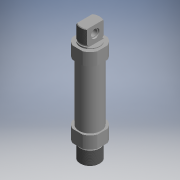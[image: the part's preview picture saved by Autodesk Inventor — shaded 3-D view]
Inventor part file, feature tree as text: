
AUTODESK INVENTOR PART (.ipt)
format: ipt  version: 2017.3 (Build 213256000, 256)  size: 256,512 bytes
history: native  units: mm (DEFAULTED — no unit token found)
features: other x70, sketch x7, revolve x3, thread x2, extrude x2, hole x2
ambient origin geometry x8: Origin, YZ Plane, XZ Plane, XY Plane, X Axis, Y Axis, Z Axis, Center Point
bodies: Solid1 (feature_tree)
feature tree (86):
  revolve  "Revolution1"  [1 undecoded]
  thread  "Thread1"  [1 undecoded]
  thread  "Thread2"  [1 undecoded]
  extrude  "Extrusion1"  TaperAngle=360.0deg  [1 undecoded]
  extrude  "Extrusion2"  TaperAngle=360.0deg  [1 undecoded]
  revolve  "Revolution2"  [1 undecoded]
  hole  "Hole1"  [1 undecoded]
  hole  "Hole2"  [1 undecoded]
  revolve  "Revolution3"  [1 undecoded]
  other  "FDT_FRONT_XY"
  other  "FDT_FRONT_YZ"
  other  "FDT_FRONT_ZX"
  other  "FDT_FRONT_X"
  other  "FDT_FRONT_Y"
  other  "FDT_FRONT_Z"
  other  "FDT_FRONT_Center"
  other  "FDT_QSFRONT_XY"
  other  "FDT_QSFRONT_YZ"
  other  "FDT_QSFRONT_ZX"
  other  "FDT_QSFRONT_X"
  other  "FDT_QSFRONT_Y"
  other  "FDT_QSFRONT_Z"
  other  "FDT_QSFRONT_Center"
  other  "FDT_QSREAR_XY"
  other  "FDT_QSREAR_YZ"
  other  "FDT_QSREAR_ZX"
  other  "FDT_QSREAR_X"
  other  "FDT_QSREAR_Y"
  other  "FDT_QSREAR_Z"
  other  "FDT_QSREAR_Center"
  other  "FDT_REAR_XY"
  other  "FDT_REAR_YZ"
  other  "FDT_REAR_ZX"
  other  "FDT_REAR_X"
  other  "FDT_REAR_Y"
  other  "FDT_REAR_Z"
  other  "FDT_REAR_Center"
  other  "FDT_SMBR1_XY"
  other  "FDT_SMBR1_YZ"
  other  "FDT_SMBR1_ZX"
  other  "FDT_SMBR1_X"
  other  "FDT_SMBR1_Y"
  other  "FDT_SMBR1_Z"
  other  "FDT_SMBR1_Center"
  other  "FDT_SMBR2_XY"
  other  "FDT_SMBR2_YZ"
  other  "FDT_SMBR2_ZX"
  other  "FDT_SMBR2_X"
  other  "FDT_SMBR2_Y"
  other  "FDT_SMBR2_Z"
  other  "FDT_SMBR2_Center"
  other  "FDT_SWIVELAXIS_XY"
  other  "FDT_SWIVELAXIS_YZ"
  other  "FDT_SWIVELAXIS_ZX"
  other  "FDT_SWIVELAXIS_X"
  other  "FDT_SWIVELAXIS_Y"
  other  "FDT_SWIVELAXIS_Z"
  other  "FDT_SWIVELAXIS_Center"
  other  "NUT_XY"
  other  "NUT_YZ"
  other  "NUT_ZX"
  other  "NUT_X"
  other  "NUT_Y"
  other  "NUT_Z"
  other  "NUT_Center"
  other  "ZR_XY"
  other  "ZR_YZ"
  other  "ZR_ZX"
  other  "ZR_X"
  other  "ZR_Y"
  other  "ZR_Z"
  other  "ZR_Center"
  other  "ZYL_XY"
  other  "ZYL_YZ"
  other  "ZYL_ZX"
  other  "ZYL_X"
  other  "ZYL_Y"
  other  "ZYL_Z"
  other  "ZYL_Center"
  sketch  "Sketch_12"  dims[d25=0.0mm d26=0.0mm d27=0.0mm d28=0.0mm d29=0.0mm d30=0.0mm]
  sketch  "Sketch_1"  dims[d0=360.0deg d1=20.03mm d2=0.0mm d3=20.03mm d4=0.0mm d5=189.5mm d6=0.0mm]
  sketch  "Sketch_124"
  sketch  "Sketch_3"  dims[d7=38.0mm d8=0.0mm d9=360.0deg]
  sketch  "Sketch5"  dims[d10=8.566mm d11=13.581mm d12=9.728mm d13=2.0mm d14=90.0deg d15=19.0mm d16=0.0mm]
  sketch  "Sketch6"  dims[d17=8.566mm d18=7.581mm d19=9.728mm d20=2.0mm d21=90.0deg d22=8.5mm d23=120.0deg d24=360.0deg]
  sketch  "Sketch_129"
note: 9 required parameter values undecoded (feature->parameter linkage not recoverable at this tier; creation-order binding heuristic only, values carry confidence <= 0.55)